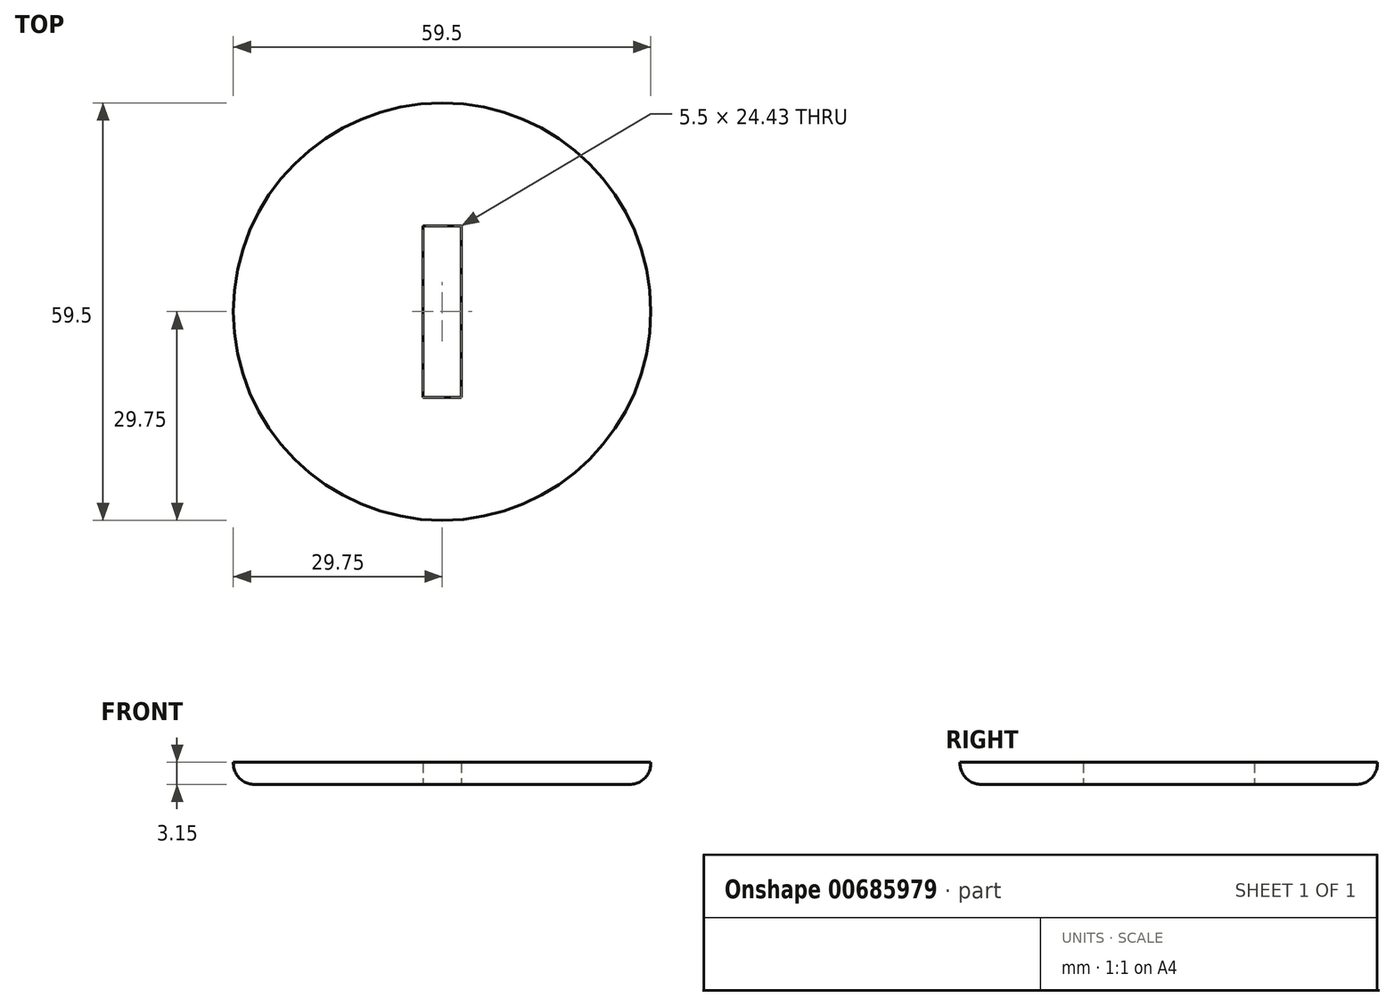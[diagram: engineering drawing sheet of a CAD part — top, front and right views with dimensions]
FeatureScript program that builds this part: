
annotation { "Feature Type Name" : "Feature", "Feature Type Description" : "" }
export const myFeature = defineFeature(function(context is Context, id is Id, definition is map)
    precondition{}
    {
        {
            var Q0;
            Q0=qCreatedBy(makeId("Top.planeOp"),FACE);
            var sketch = newSketch(context, id + "F0", { "sketchPlane" : qUnion([Q0])});
            skCircle(sketch, "E0", {"center": v(0, 0) * mm, "radius": 29.75 * mm});
            skSolve(sketch);
        }
        {
            var Q0;
            Q0=qCreatedBy(makeId("Top.planeOp"),FACE);
            var sketch = newSketch(context, id + "F1", { "sketchPlane" : qUnion([Q0])});
            skLineSegment(sketch, "E1.bottom", {"start": v(-2.75, 12.21) * mm, "end": v(2.75, 12.21) * mm});
            skLineSegment(sketch, "E1.top", {"start": v(-2.75, -12.21) * mm, "end": v(2.75, -12.21) * mm});
            skLineSegment(sketch, "E1.left", {"start": v(-2.75, 12.21) * mm, "end": v(-2.75, -12.21) * mm});
            skLineSegment(sketch, "E1.right", {"start": v(2.75, 12.21) * mm, "end": v(2.75, -12.21) * mm});
            skPoint(sketch, "E1.middle", {"position": v(0, 0) * mm});
            skSolve(sketch);
        }
        {
            var Q0;
            Q0=makeQuery(id+"F0.imprint","IMPRINT",FACE,{"disambiguationData":[TD([[makeQuery(id+"F0.imprint","IMPRINT",EDGE,{"derivedFrom":sQuery(id+"F0.wireOp",EDGE,"E0")}),1.0]])]});
            extrude(context, id + "F2", {"entities" : qUnion([Q0]), "depth" : 3.15 * mm, "offsetDistance" : 25 * mm});
        }
        {
            var Q0;
            Q0 = qSketchRegion(id + "F1", true);
            extrude(context, id + "F3", {"entities" : qUnion([Q0]), "operationType" : NewBodyOperationType.REMOVE, "depth" : 3.15 * mm, "offsetDistance" : 25 * mm});
        }
        {
            var Q0;
            Q0=makeQuery(id+"F2.opExtrude","CAP_EDGE",EDGE,{"disambiguationData":[OSD([sQuery(id+"F0.wireOp",EDGE,"E0")])],"isStart":true});
            fillet(context, id + "F4", {"entities" : qUnion([Q0]), "tangentPropagation" : true, "radius" : 3 * mm, "defaultsChanged" : true, "vertexSettings" : [], "allowEdgeOverflow" : false});
        }
    });
